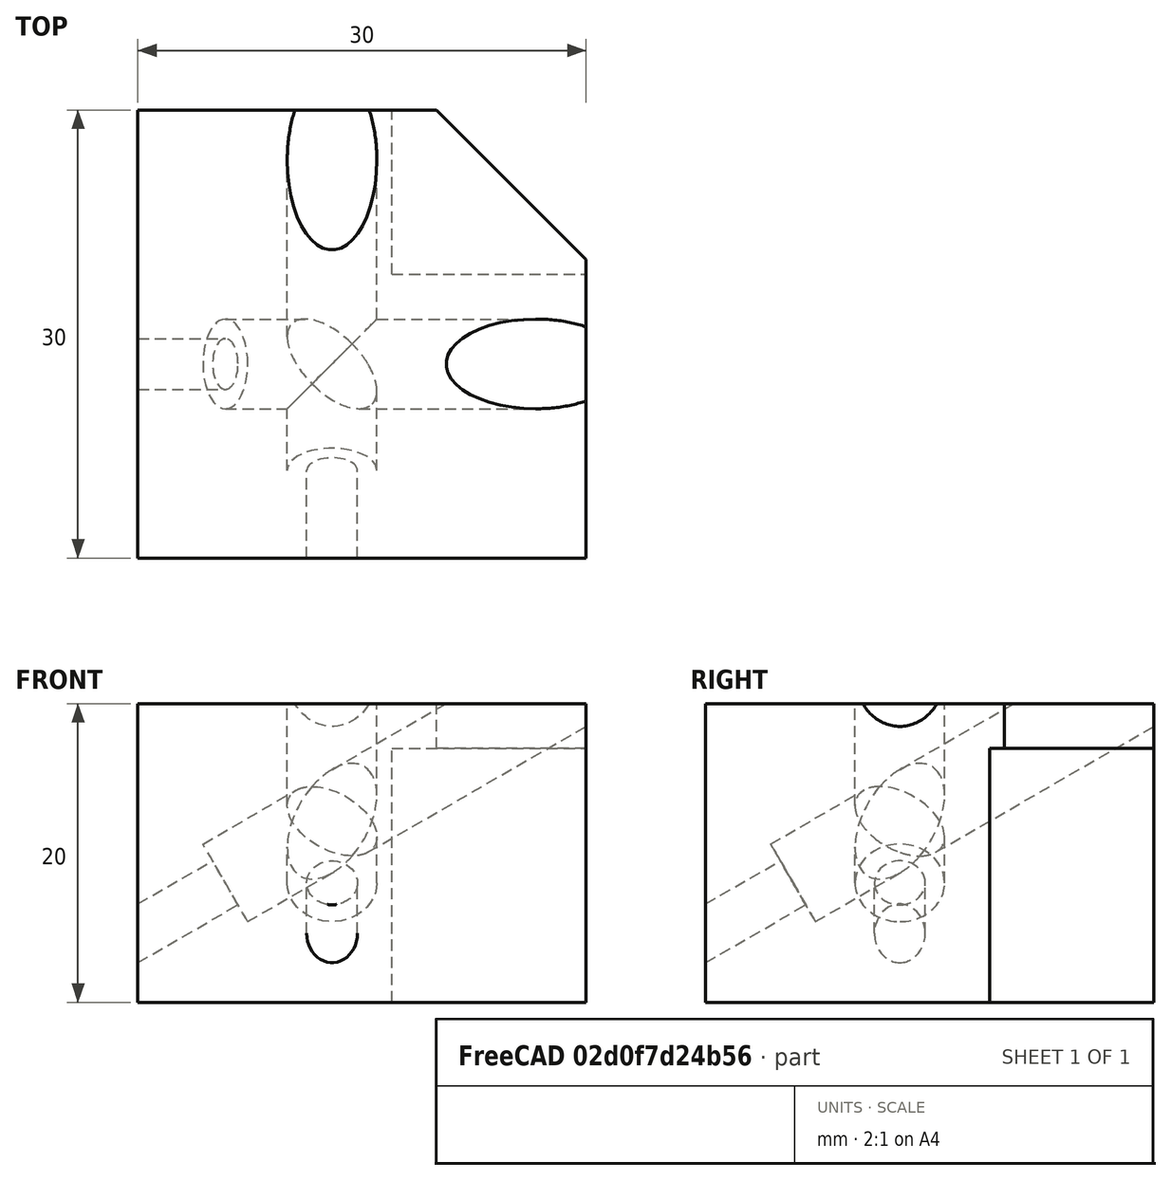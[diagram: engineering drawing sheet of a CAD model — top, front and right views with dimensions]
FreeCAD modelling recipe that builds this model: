
FCSTD DOCUMENT  (FreeCAD 0.17R13541 (Git))
Label: picture-frame-clamp
License: All rights reserved
LicenseURL: http://en.wikipedia.org/wiki/All_rights_reserved
objects: Part::MultiFuse×3, Part::Box×2, Part::Cut×2, Part::Cylinder×2, Part::Chamfer×1
note: 10 computed .brp shape members not serialized (recipe doc carries the construction recipe); baked Part::Feature solids carry a one-line shape summary decoded from their .brp

FEATURE [Part::Box] Box  label="Cube"
  AttacherType = Attacher::AttachEngine3D
  Height = 20
  Length = 30
  Width = 30
FEATURE [Part::Chamfer] Chamfer
  Base = -> Box
  Edges = 1 edges r=10: [Edge7]
FEATURE [Part::Box] Box001  label="Cube001"
  AttacherType = Attacher::AttachEngine3D
  Height = 20
  Length = 18
  Placement = pos=(17,19,-3) rot=(0,0,1;0rad)
  Width = 19
FEATURE [Part::Cut] Cut
  Base = -> Chamfer
  Tool = -> Box001
FEATURE [Part::Cylinder] Cylinder
  Angle = 360
  AttacherType = Attacher::AttachEngine3D
  Height = 40
  Radius = 1.7
FEATURE [Part::Cylinder] Cylinder001
  Angle = 360
  AttacherType = Attacher::AttachEngine3D
  Height = 40
  Placement = pos=(0,0,16) rot=(0,0,1;0rad)
  Radius = 3
FEATURE [Part::MultiFuse] Fusion  label="screw"
  Placement = pos=(-8,13,0) rot=(0,1,0;1.0472rad)
  Shapes = -> [Cylinder,Cylinder001]
FEATURE [Part::MultiFuse] Fusion001  label="screw001"
  Placement = pos=(13,-8,0) rot=(1,0,0;-1.0472rad)
  Shapes = -> [Cylinder,Cylinder001]
FEATURE [Part::MultiFuse] Fusion002
  Shapes = -> [Fusion,Fusion001]
FEATURE [Part::Cut] Cut001
  Base = -> Cut
  Tool = -> Fusion002
